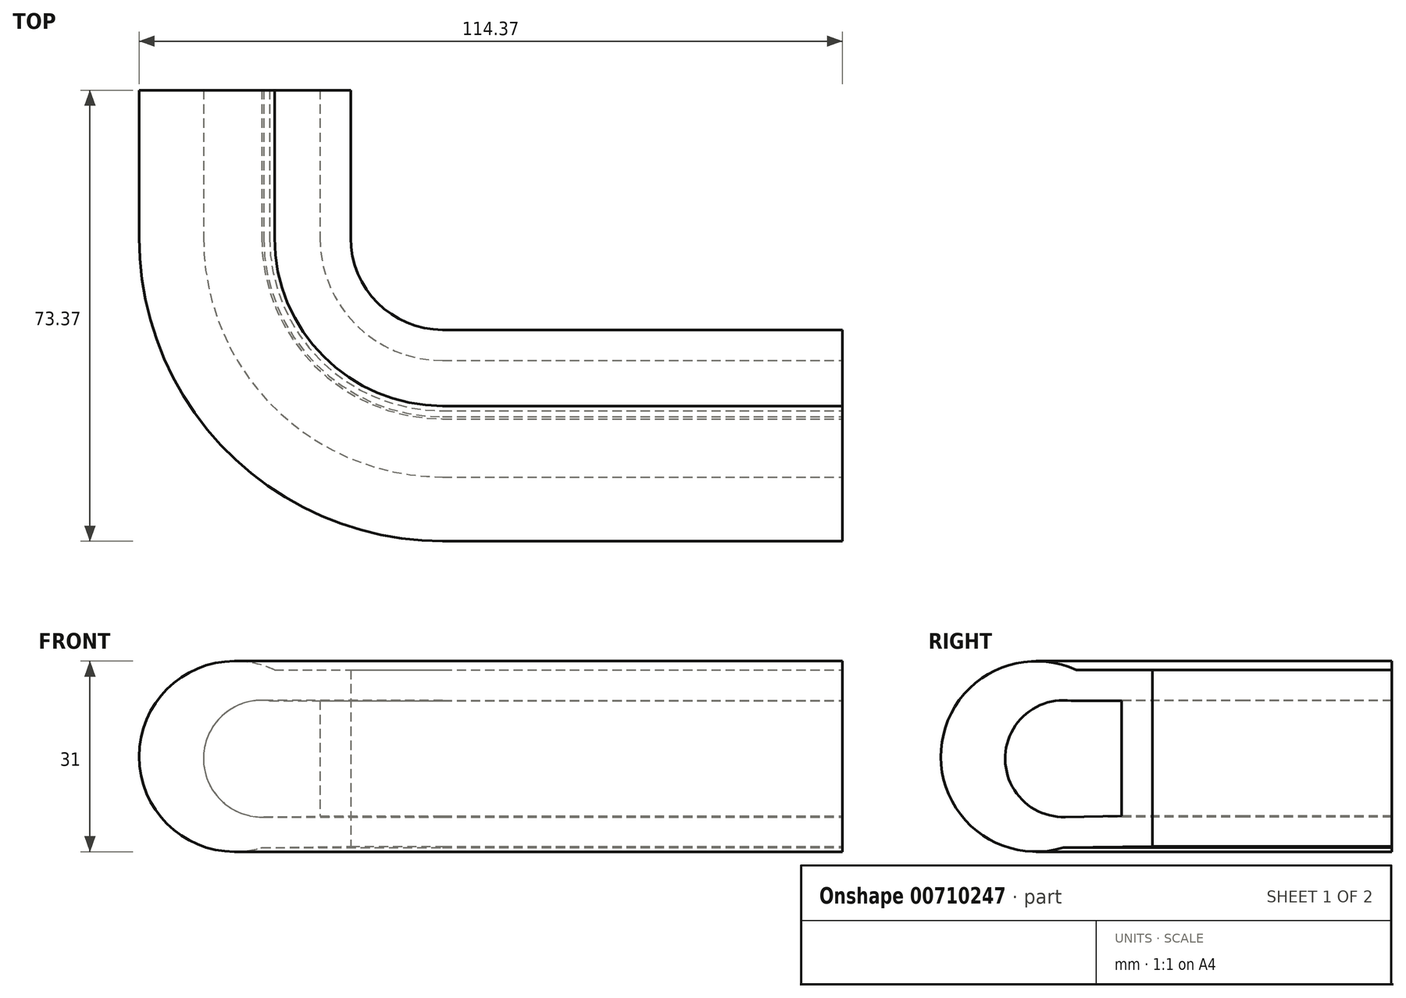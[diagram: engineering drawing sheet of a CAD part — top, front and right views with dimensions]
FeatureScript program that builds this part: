
annotation { "Feature Type Name" : "Feature", "Feature Type Description" : "" }
export const myFeature = defineFeature(function(context is Context, id is Id, definition is map)
    precondition{}
    {
        {
            var Q0;
            Q0=qCreatedBy(makeId("Top.planeOp"),FACE);
            var sketch = newSketch(context, id + "F0", { "sketchPlane" : qUnion([Q0])});
            skLineSegment(sketch, "E0", {"start": v(-30.2, 0) * mm, "end": v(-30.2, -24) * mm});
            skLineSegment(sketch, "E1", {"start": v(-20.2, -34) * mm, "end": v(44.8, -34) * mm});
            skPoint(sketch, "E2.visualSharp", {"position": v(-30.2, -34) * mm});
            skArc(sketch, "E2.filletArc", {"start": v(-30.2, -24) * mm, "mid": v(-27.27, -31.07) * mm, "end": v(-20.2, -34) * mm});
            skSolve(sketch);
        }
        {
            var Q0;
            Q0=qCreatedBy(makeId("Right.planeOp"),FACE);
            var sketch = newSketch(context, id + "F1", { "sketchPlane" : qUnion([Q0])});
            skArc(sketch, "E3", {"start": v(-52.15, 41.38) * mm, "mid": v(-62.9, 32.45) * mm, "end": v(-53.12, 22.47) * mm});
            skLineSegment(sketch, "E4", {"start": v(-53.4, 22.46) * mm, "end": v(-43.97, 22.6) * mm});
            skLineSegment(sketch, "E5", {"start": v(-54.66, 41.38) * mm, "end": v(-43.97, 41.38) * mm});
            skLineSegment(sketch, "E6", {"start": v(-43.97, 41.38) * mm, "end": v(-43.97, 22.6) * mm});
            skArc(sketch, "E7.trimOffspring", {"start": v(-51.35, 46.38) * mm, "mid": v(-73.33, 33.44) * mm, "end": v(-53.45, 17.46) * mm});
            skLineSegment(sketch, "E8.0", {"start": v(-53.77, 17.46) * mm, "end": v(-38.97, 17.68) * mm});
            skLineSegment(sketch, "E8.1", {"start": v(-38.97, 46.38) * mm, "end": v(-38.97, 17.68) * mm});
            skLineSegment(sketch, "E8.2", {"start": v(-54.12, 46.38) * mm, "end": v(-38.97, 46.38) * mm});
            skSolve(sketch);
        }
        {
            var Q0;
            {var subQ6=sQuery(id+"F1.wireOp",EDGE,"E6");Q0=makeQuery(id+"F1.imprint","IMPRINT",FACE,{"disambiguationData":[TD([[makeQuery(id+"F1.imprint","IMPRINT",EDGE,{"derivedFrom":subQ6}),1.0]])]});}
            var Q1;
            Q1=sQuery(id+"F0.wireOp",EDGE,"E1");
            var Q2;
            Q2=sQuery(id+"F0.wireOp",EDGE,"E2.filletArc");
            var Q3;
            Q3=sQuery(id+"F0.wireOp",EDGE,"E0");
            sweep(context, id + "F2", {"profiles" : qUnion([Q0]), "path" : qUnion([Q1, Q2, Q3])});
        }
    });
